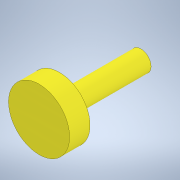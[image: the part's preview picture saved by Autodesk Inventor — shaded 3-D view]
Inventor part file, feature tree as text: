
AUTODESK INVENTOR PART (.ipt)
format: ipt  version: 2021 (Build 250183000, 183)  size: 107,520 bytes
history: native  units: in
note: dims shown in document units (in); Inventor stores cm internally (conversion verified against a paired STEP export)
features: extrude x3, sketch x3, other x3, plane x2
ambient origin geometry x8: Origin, YZ Plane, XZ Plane, XY Plane, X Axis, Y Axis, Z Axis, Center Point
bodies: Solid1 (feature_tree)
feature tree (11):
  plane  "Work Plane1"
  extrude  "Extrusion1"  Depth=2.0in TaperAngle=0.0deg
  extrude  "Extrusion2"  Depth=3.0in
  extrude  "Extrusion3"  [1 undecoded]
  plane  "Work Plane2"
  sketch  "Sketch1"  dims[d0=1.0in d1=2.0in d2=0.0in]
  sketch  "Sketch2"  dims[d3=2.0in d4=0.0in d6=3.0in]
  sketch  "Sketch4"  dims[d7=1.0in d8=0.0in]
  parser-record x1  (decoder bookkeeping rows leaked as tree rows — omitted from the tree; the rows remain in map.json)
  other  "Clutch02.iam"
  other  "clutch02-simplyGearDisk:1"
note: 1 required parameter value undecoded (feature->parameter linkage not recoverable at this tier; creation-order binding heuristic only, values carry confidence <= 0.55)
note: 1 file-system path scrubbed to <path> (originals preserved in map.json)
